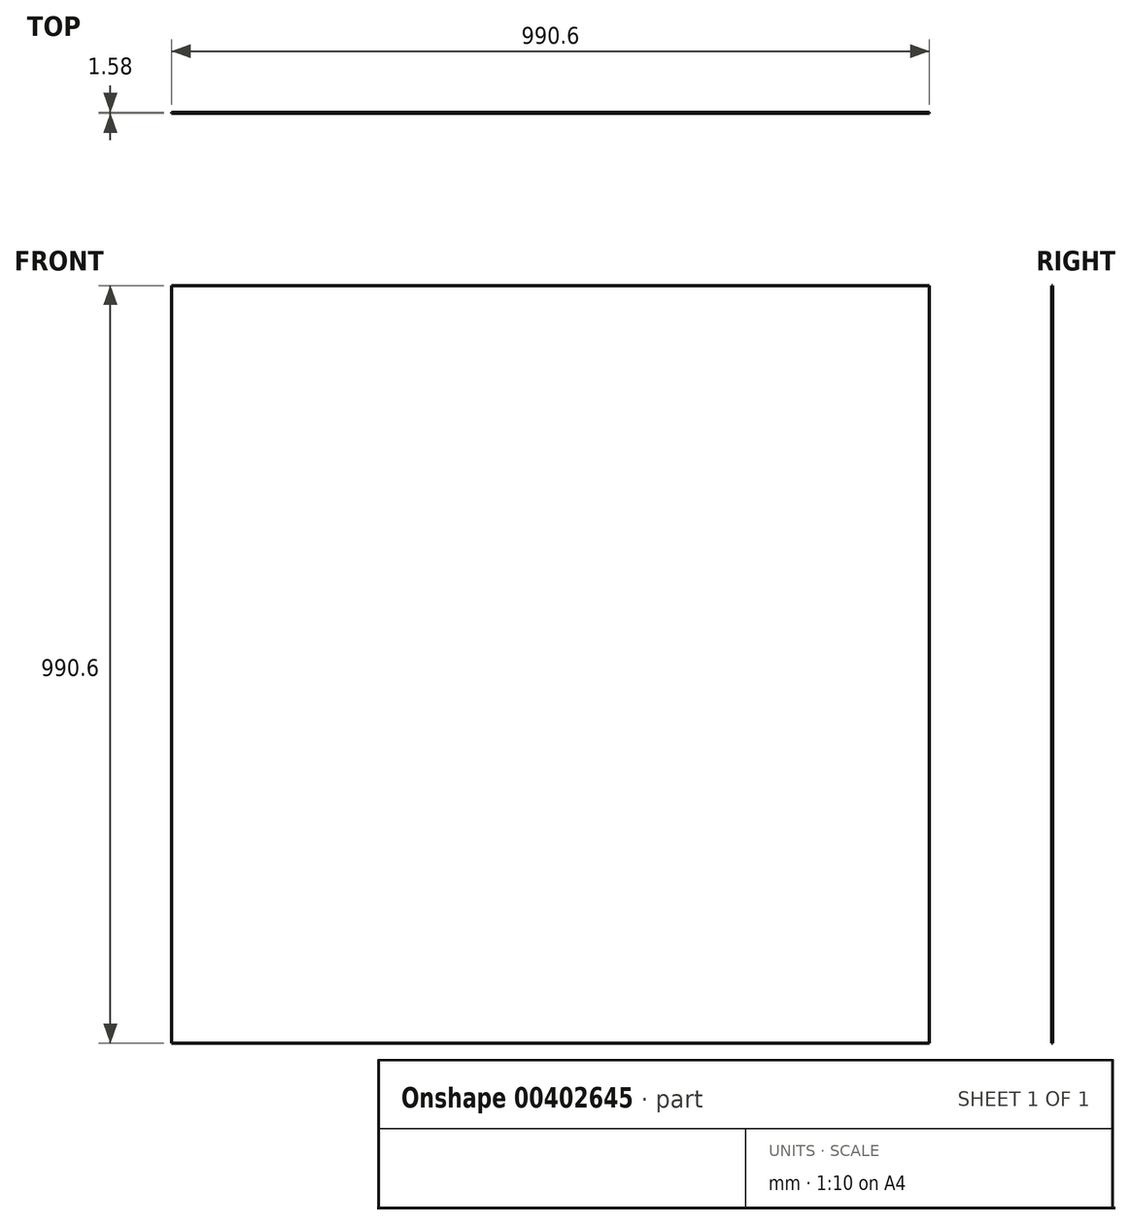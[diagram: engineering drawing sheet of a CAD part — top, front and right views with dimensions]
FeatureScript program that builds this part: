
annotation { "Feature Type Name" : "Feature", "Feature Type Description" : "" }
export const myFeature = defineFeature(function(context is Context, id is Id, definition is map)
    precondition{}
    {
        {
            var Q0;
            Q0=qCreatedBy(makeId("Front.planeOp"),FACE);
            var sketch = newSketch(context, id + "F0", { "sketchPlane" : qUnion([Q0])});
            skLineSegment(sketch, "E0.bottom", {"start": v(495.3, 495.3) * mm, "end": v(-495.3, 495.3) * mm});
            skLineSegment(sketch, "E0.top", {"start": v(495.3, -495.3) * mm, "end": v(-495.3, -495.3) * mm});
            skLineSegment(sketch, "E0.left", {"start": v(495.3, 495.3) * mm, "end": v(495.3, -495.3) * mm});
            skLineSegment(sketch, "E0.right", {"start": v(-495.3, 495.3) * mm, "end": v(-495.3, -495.3) * mm});
            skPoint(sketch, "E0.middle", {"position": v(0, 0) * mm});
            skSolve(sketch);
        }
        {
            var Q0;
            Q0 = qSketchRegion(id + "F0", true);
            extrude(context, id + "F1", {"entities" : qUnion([Q0]), "depth" : 1.59 * mm, "symmetric" : true});
        }
    });
